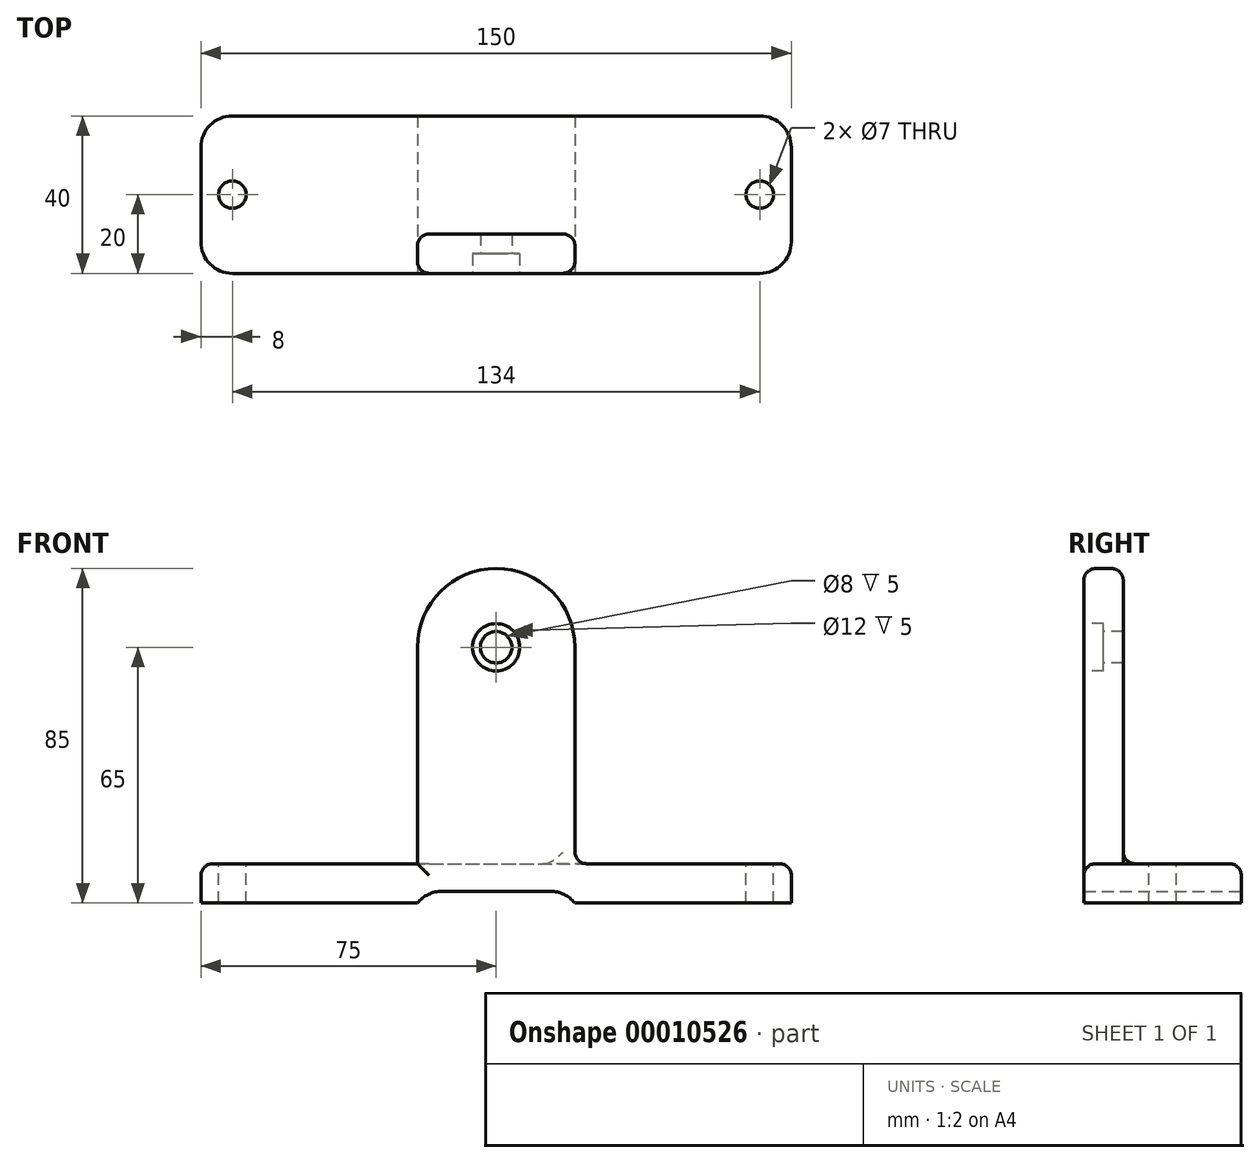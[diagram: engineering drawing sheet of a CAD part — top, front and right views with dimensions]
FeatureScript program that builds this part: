
annotation { "Feature Type Name" : "Feature", "Feature Type Description" : "" }
export const myFeature = defineFeature(function(context is Context, id is Id, definition is map)
    precondition{}
    {
        {
            var Q0;
            Q0=qCreatedBy(makeId("Top.planeOp"),FACE);
            var sketch = newSketch(context, id + "F0", { "sketchPlane" : qUnion([Q0])});
            skLineSegment(sketch, "E0.bottom", {"start": v(0, 0) * mm, "end": v(150, 0) * mm});
            skLineSegment(sketch, "E0.top", {"start": v(0, 40) * mm, "end": v(150, 40) * mm});
            skLineSegment(sketch, "E0.left", {"start": v(0, 0) * mm, "end": v(0, 40) * mm});
            skLineSegment(sketch, "E0.right", {"start": v(150, 0) * mm, "end": v(150, 40) * mm});
            skSolve(sketch);
        }
        {
            var Q0;
            Q0=qSketchRegion(id+"F0",true);
            extrude(context, id + "F1", {"entities" : qUnion([Q0]), "depth" : 10 * mm});
        }
        {
            var Q0;
            Q0=makeQuery(id+"F1.opExtrude","SWEPT_FACE",FACE,{"disambiguationData":[OSD([sQuery(id+"F0.wireOp",EDGE,"E0.bottom")])]});
            var sketch = newSketch(context, id + "F2", { "sketchPlane" : qUnion([Q0])});
            skLineSegment(sketch, "E1", {"start": v(55, 0) * mm, "end": v(55, 65) * mm});
            skArc(sketch, "E2", {"start": v(55, 65) * mm, "mid": v(75, 85) * mm, "end": v(95, 65) * mm});
            skLineSegment(sketch, "E3", {"start": v(95, 65) * mm, "end": v(95, 0) * mm});
            skLineSegment(sketch, "E4", {"start": v(95, 0) * mm, "end": v(55, 0) * mm});
            skSolve(sketch);
        }
        {
            var Q0;
            Q0=qSketchRegion(id+"F2",true);
            extrude(context, id + "F3", {"entities" : qUnion([Q0]), "operationType" : NewBodyOperationType.ADD, "oppositeDirection" : true, "depth" : 10 * mm});
        }
        {
            var Q0;
            Q0=makeQuery(id+"F3.boolean.opBoolean","MERGE",FACE,{"derivedFrom":[makeQuery(id+"F1.opExtrude","SWEPT_FACE",FACE,{"disambiguationData":[OSD([sQuery(id+"F0.wireOp",EDGE,"E0.bottom")])]}),makeQuery(id+"F3.opExtrude","CAP_FACE",FACE,{"disambiguationData":[OSD([sQuery(id+"F2.wireOp",EDGE,"E1"),sQuery(id+"F2.wireOp",EDGE,"E2"),sQuery(id+"F2.wireOp",EDGE,"E3"),sQuery(id+"F2.wireOp",EDGE,"E4")])],"isStart":true})]});
            var sketch = newSketch(context, id + "F4", { "sketchPlane" : qUnion([Q0])});
            skLineSegment(sketch, "E5.bottom", {"start": v(55, 0) * mm, "end": v(95, 0) * mm});
            skLineSegment(sketch, "E5.top", {"start": v(55, 3) * mm, "end": v(95, 3) * mm});
            skLineSegment(sketch, "E5.left", {"start": v(55, 0) * mm, "end": v(55, 3) * mm});
            skLineSegment(sketch, "E5.right", {"start": v(95, 0) * mm, "end": v(95, 3) * mm});
            skSolve(sketch);
        }
        {
            var Q0;
            Q0=qSketchRegion(id+"F4",true);
            extrude(context, id + "F5", {"entities" : qUnion([Q0]), "operationType" : NewBodyOperationType.REMOVE, "endBound" : BoundingType.THROUGH_ALL, "oppositeDirection" : true, "depth" : 25 * mm});
        }
        {
            var Q0;
            Q0=makeQuery(id+"F3.boolean.opBoolean","MERGE",FACE,{"derivedFrom":[makeQuery(id+"F1.opExtrude","SWEPT_FACE",FACE,{"disambiguationData":[OSD([sQuery(id+"F0.wireOp",EDGE,"E0.bottom")])]}),makeQuery(id+"F3.opExtrude","CAP_FACE",FACE,{"disambiguationData":[OSD([sQuery(id+"F2.wireOp",EDGE,"E1"),sQuery(id+"F2.wireOp",EDGE,"E2"),sQuery(id+"F2.wireOp",EDGE,"E3"),sQuery(id+"F2.wireOp",EDGE,"E4")])],"isStart":true})]});
            var sketch = newSketch(context, id + "F6", { "sketchPlane" : qUnion([Q0])});
            skCircle(sketch, "E6", {"center": v(75, 65) * mm, "radius": 4 * mm});
            skSolve(sketch);
        }
        {
            var Q0;
            Q0=sQuery(id+"F6.wireOp",VERTEX,"E6.center");
            var Q1;
            Q1=makeQuery(id+"F1.opExtrude","SWEPT_BODY",BODY,{"disambiguationData":[OSD([sQuery(id+"F0.wireOp",EDGE,"E0.bottom"),sQuery(id+"F0.wireOp",EDGE,"E0.top"),sQuery(id+"F0.wireOp",EDGE,"E0.left"),sQuery(id+"F0.wireOp",EDGE,"E0.right")])]});
            hole(context, id + "F7", {"style" : HoleStyle.C_BORE, "endStyle" : HoleEndStyle.THROUGH, "holeDiameter" : 8 * mm, "cBoreDiameter" : 12 * mm, "cBoreDepth" : 5 * mm, "tappedDepth" : 12 * mm, "tapClearance" : 3, "locations" : qUnion([Q0]), "scope" : qUnion([Q1])});
        }
        {
            var Q0;
            Q0=makeQuery(id+"F1.opExtrude","SWEPT_EDGE",EDGE,{"disambiguationData":[OSD([sQuery(id+"F0.wireOp",EDGE,"E0.top"),sQuery(id+"F0.wireOp",EDGE,"E0.right")])]});
            var Q1;
            Q1=makeQuery(id+"F1.opExtrude","SWEPT_EDGE",EDGE,{"disambiguationData":[OSD([sQuery(id+"F0.wireOp",EDGE,"E0.bottom"),sQuery(id+"F0.wireOp",EDGE,"E0.right")])]});
            var Q2;
            Q2=makeQuery(id+"F1.opExtrude","SWEPT_EDGE",EDGE,{"disambiguationData":[OSD([sQuery(id+"F0.wireOp",EDGE,"E0.bottom"),sQuery(id+"F0.wireOp",EDGE,"E0.left")])]});
            var Q3;
            Q3=makeQuery(id+"F1.opExtrude","SWEPT_EDGE",EDGE,{"disambiguationData":[OSD([sQuery(id+"F0.wireOp",EDGE,"E0.top"),sQuery(id+"F0.wireOp",EDGE,"E0.left")])]});
            var Q4;
            Q4=makeQuery(id+"F5.boolean.opBoolean","COPY",EDGE,{"derivedFrom":makeQuery(id+"F5.opExtrude","SWEPT_EDGE",EDGE,{"disambiguationData":[OSD([sQuery(id+"F4.wireOp",EDGE,"E5.top"),sQuery(id+"F4.wireOp",EDGE,"E5.right")])]})});
            var Q5;
            Q5=makeQuery(id+"F5.boolean.opBoolean","COPY",EDGE,{"derivedFrom":makeQuery(id+"F5.opExtrude","SWEPT_EDGE",EDGE,{"disambiguationData":[OSD([sQuery(id+"F4.wireOp",EDGE,"E5.top"),sQuery(id+"F4.wireOp",EDGE,"E5.left")])]})});
            fillet(context, id + "F8", {"entities" : qUnion([Q0, Q1, Q2, Q3, Q4, Q5]), "radius" : 8 * mm, "tangentPropagation" : true, "allowEdgeOverflow" : false});
        }
        {
            var Q0;
            Q0=makeQuery(id+"F1.opExtrude","CAP_FACE",FACE,{"disambiguationData":[OSD([sQuery(id+"F0.wireOp",EDGE,"E0.bottom"),sQuery(id+"F0.wireOp",EDGE,"E0.top"),sQuery(id+"F0.wireOp",EDGE,"E0.left"),sQuery(id+"F0.wireOp",EDGE,"E0.right")])],"isStart":false});
            var sketch = newSketch(context, id + "F9", { "sketchPlane" : qUnion([Q0])});
            skPoint(sketch, "E7", {"position": v(142, 20) * mm});
            skPoint(sketch, "E8", {"position": v(8, 20) * mm});
            skSolve(sketch);
        }
        {
            var Q0;
            Q0=sQuery(id+"F9.wireOp",VERTEX,"E7");
            var Q1;
            Q1=sQuery(id+"F9.wireOp",VERTEX,"E8");
            var Q2;
            Q2=makeQuery(id+"F1.opExtrude","SWEPT_BODY",BODY,{"disambiguationData":[OSD([sQuery(id+"F0.wireOp",EDGE,"E0.bottom"),sQuery(id+"F0.wireOp",EDGE,"E0.top"),sQuery(id+"F0.wireOp",EDGE,"E0.left"),sQuery(id+"F0.wireOp",EDGE,"E0.right")])]});
            hole(context, id + "F10", {"style" : HoleStyle.SIMPLE, "endStyle" : HoleEndStyle.THROUGH, "holeDiameter" : 7 * mm, "isTappedThrough" : true, "tappedDepth" : 12 * mm, "tapClearance" : 3, "locations" : qUnion([Q0, Q1]), "scope" : qUnion([Q2])});
        }
        {
            var Q0;
            Q0=makeQuery(id+"F3.opExtrude","CAP_EDGE",EDGE,{"disambiguationData":[OSD([sQuery(id+"F2.wireOp",EDGE,"E3")])],"isStart":false});
            var Q1;
            Q1=makeQuery(id+"F3.opExtrude","CAP_EDGE",EDGE,{"disambiguationData":[OSD([sQuery(id+"F2.wireOp",EDGE,"E3")])],"isStart":true});
            var Q2;
            {var subQ1=sQuery(id+"F0.wireOp",EDGE,"E0.right");var subQ2=sQuery(id+"F0.wireOp",EDGE,"E0.bottom");Q2=makeQuery(id+"F3.boolean.opBoolean","SPLIT",EDGE,{"disambiguationData":[TD([makeQuery(id+"F1.opExtrude","SWEPT_FACE",FACE,{"disambiguationData":[OSD([subQ1])]})])],"derivedFrom":makeQuery(id+"F1.opExtrude","CAP_EDGE",EDGE,{"disambiguationData":[OSD([subQ2])],"isStart":false})});}
            var Q3;
            Q3=makeQuery(id+"F3.boolean.opBoolean","INTERSECT",EDGE,{"derivedFrom":[makeQuery(id+"F1.opExtrude","CAP_FACE",FACE,{"disambiguationData":[OSD([sQuery(id+"F0.wireOp",EDGE,"E0.bottom"),sQuery(id+"F0.wireOp",EDGE,"E0.top"),sQuery(id+"F0.wireOp",EDGE,"E0.left"),sQuery(id+"F0.wireOp",EDGE,"E0.right")])],"isStart":false}),makeQuery(id+"F3.opExtrude","SWEPT_FACE",FACE,{"disambiguationData":[OSD([sQuery(id+"F2.wireOp",EDGE,"E3")])]})]});
            fillet(context, id + "F11", {"entities" : qUnion([Q0, Q1, Q2, Q3]), "radius" : 3 * mm, "tangentPropagation" : true, "allowEdgeOverflow" : false});
        }
    });
